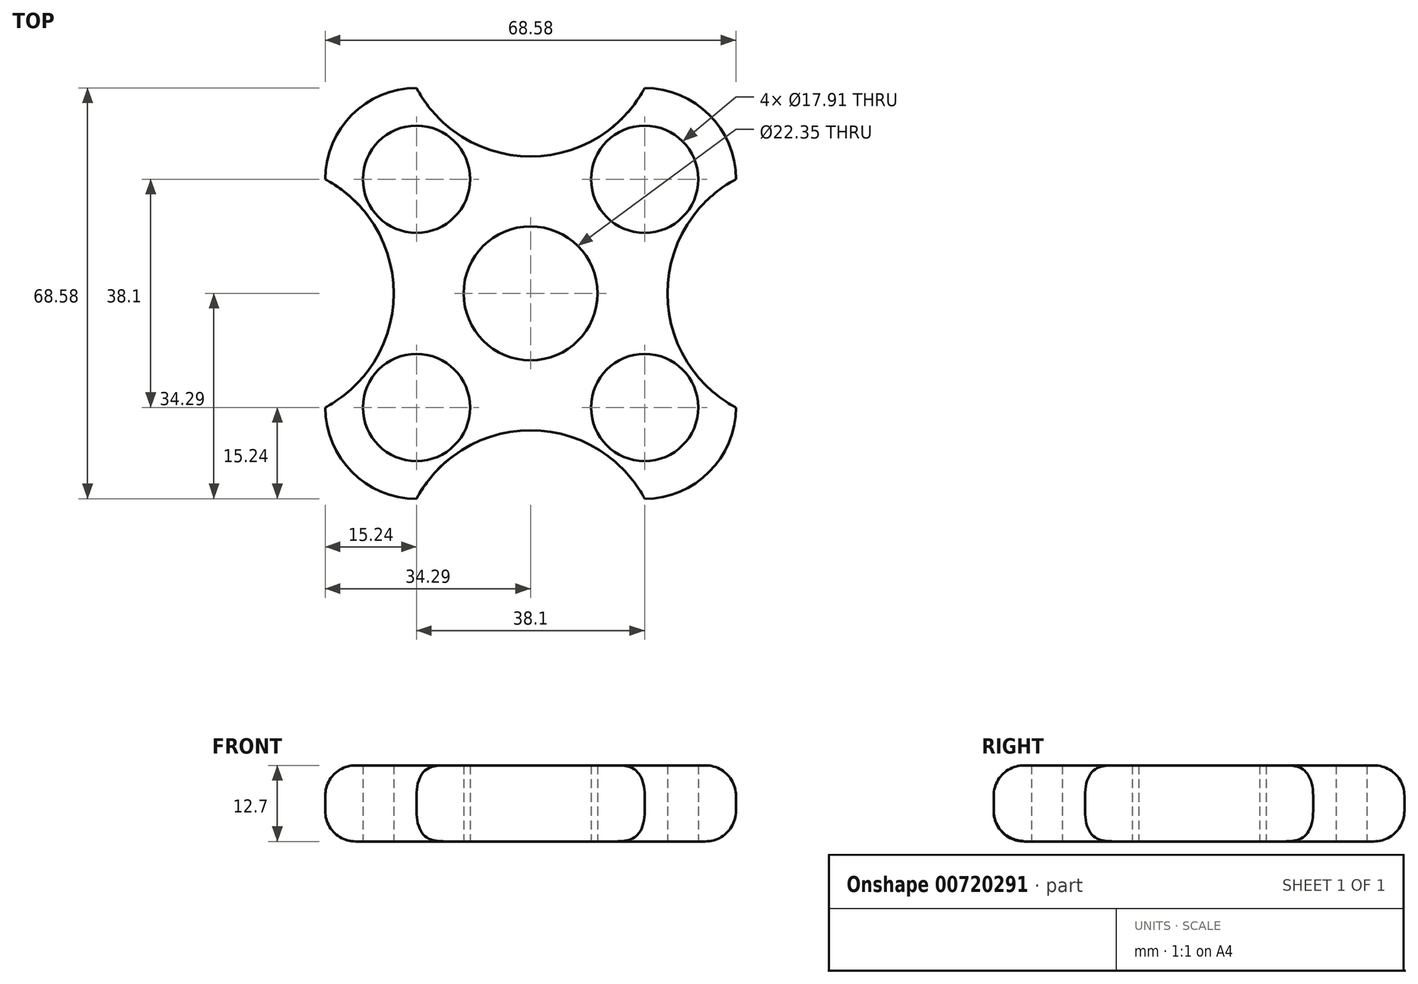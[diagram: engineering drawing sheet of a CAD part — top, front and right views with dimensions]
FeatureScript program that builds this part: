
annotation { "Feature Type Name" : "Feature", "Feature Type Description" : "" }
export const myFeature = defineFeature(function(context is Context, id is Id, definition is map)
    precondition{}
    {
        {
            var Q0;
            Q0=qCreatedBy(makeId("Top.planeOp"),FACE);
            var sketch = newSketch(context, id + "F0", { "sketchPlane" : qUnion([Q0])});
            skCircle(sketch, "E0", {"center": v(0, 0) * mm, "radius": 11.18 * mm});
            skLineSegment(sketch, "E1", {"start": v(0, 0) * mm, "end": v(19.05, 0) * mm, "construction": true});
            skLineSegment(sketch, "E2", {"start": v(19.05, 0) * mm, "end": v(19.05, 19.05) * mm, "construction": true});
            skLineSegment(sketch, "E3", {"start": v(0, 0) * mm, "end": v(-19.05, 0) * mm, "construction": true});
            skLineSegment(sketch, "E4", {"start": v(-19.05, 0) * mm, "end": v(-19.05, 19.05) * mm, "construction": true});
            skLineSegment(sketch, "E5", {"start": v(19.05, 0) * mm, "end": v(19.05, -19.05) * mm, "construction": true});
            skLineSegment(sketch, "E6", {"start": v(-19.05, 0) * mm, "end": v(-19.05, -19.05) * mm, "construction": true});
            skCircle(sketch, "E7", {"center": v(19.05, 19.05) * mm, "radius": 8.95 * mm});
            skCircle(sketch, "E8", {"center": v(-19.05, 19.05) * mm, "radius": 8.95 * mm});
            skCircle(sketch, "E9", {"center": v(-19.05, -19.05) * mm, "radius": 8.95 * mm});
            skCircle(sketch, "E10", {"center": v(19.05, -19.05) * mm, "radius": 8.95 * mm});
            skLineSegment(sketch, "E11", {"start": v(-19.05, -19.05) * mm, "end": v(-19.05, -34.3) * mm, "construction": true});
            skLineSegment(sketch, "E12", {"start": v(19.05, -19.05) * mm, "end": v(34.3, -19.05) * mm, "construction": true});
            skLineSegment(sketch, "E13", {"start": v(19.05, 19.05) * mm, "end": v(19.05, 34.3) * mm, "construction": true});
            skLineSegment(sketch, "E14", {"start": v(-19.05, 19.05) * mm, "end": v(-34.29, 19.05) * mm, "construction": true});
            skArc(sketch, "E15", {"start": v(-19.05, 34.3) * mm, "mid": v(-29.83, 29.83) * mm, "end": v(-34.29, 19.05) * mm});
            skArc(sketch, "E16", {"start": v(-34.29, -19.05) * mm, "mid": v(-29.83, -29.83) * mm, "end": v(-19.05, -34.3) * mm});
            skArc(sketch, "E17", {"start": v(19.05, -34.3) * mm, "mid": v(29.83, -29.83) * mm, "end": v(34.3, -19.05) * mm});
            skArc(sketch, "E18", {"start": v(34.3, 19.05) * mm, "mid": v(29.83, 29.83) * mm, "end": v(19.05, 34.3) * mm});
            skArc(sketch, "E19", {"start": v(19.05, -34.3) * mm, "mid": v(0, -22.86) * mm, "end": v(-19.05, -34.3) * mm});
            skArc(sketch, "E20", {"start": v(34.3, 19.05) * mm, "mid": v(22.86, 0) * mm, "end": v(34.3, -19.05) * mm});
            skArc(sketch, "E21", {"start": v(-19.05, 34.3) * mm, "mid": v(0, 22.86) * mm, "end": v(19.05, 34.3) * mm});
            skArc(sketch, "E22", {"start": v(-34.3, -19.05) * mm, "mid": v(-22.86, 0) * mm, "end": v(-34.3, 19.05) * mm});
            skSolve(sketch);
        }
        {
            var Q0;
            Q0=makeQuery(id+"F0.imprint","IMPRINT",FACE,{"disambiguationData":[TD([[makeQuery(id+"F0.imprint","IMPRINT",EDGE,{"derivedFrom":sQuery(id+"F0.wireOp",EDGE,"E0")}),-1.0]])]});
            extrude(context, id + "F1", {"entities" : qUnion([Q0]), "depth" : 12.7 * mm, "offsetDistance" : 25.4 * mm});
        }
        {
            var Q0;
            Q0=makeQuery(id+"F1.opExtrude","CAP_EDGE",EDGE,{"disambiguationData":[OSD([sQuery(id+"F0.wireOp",EDGE,"E18")])],"isStart":true});
            var Q1;
            Q1=makeQuery(id+"F1.opExtrude","CAP_EDGE",EDGE,{"disambiguationData":[OSD([sQuery(id+"F0.wireOp",EDGE,"E17")])],"isStart":true});
            var Q2;
            Q2=makeQuery(id+"F1.opExtrude","CAP_EDGE",EDGE,{"disambiguationData":[OSD([sQuery(id+"F0.wireOp",EDGE,"E16")])],"isStart":true});
            var Q3;
            Q3=makeQuery(id+"F1.opExtrude","CAP_EDGE",EDGE,{"disambiguationData":[OSD([sQuery(id+"F0.wireOp",EDGE,"E15")])],"isStart":true});
            var Q4;
            Q4=makeQuery(id+"F1.opExtrude","CAP_EDGE",EDGE,{"disambiguationData":[OSD([sQuery(id+"F0.wireOp",EDGE,"E15")])],"isStart":false});
            var Q5;
            Q5=makeQuery(id+"F1.opExtrude","CAP_EDGE",EDGE,{"disambiguationData":[OSD([sQuery(id+"F0.wireOp",EDGE,"E18")])],"isStart":false});
            var Q6;
            Q6=makeQuery(id+"F1.opExtrude","CAP_EDGE",EDGE,{"disambiguationData":[OSD([sQuery(id+"F0.wireOp",EDGE,"E17")])],"isStart":false});
            var Q7;
            Q7=makeQuery(id+"F1.opExtrude","CAP_EDGE",EDGE,{"disambiguationData":[OSD([sQuery(id+"F0.wireOp",EDGE,"E16")])],"isStart":false});
            fillet(context, id + "F2", {"entities" : qUnion([Q0, Q1, Q2, Q3, Q4, Q5, Q6, Q7]), "radius" : 5.08 * mm, "tangentPropagation" : true, "allowEdgeOverflow" : false});
        }
    });
